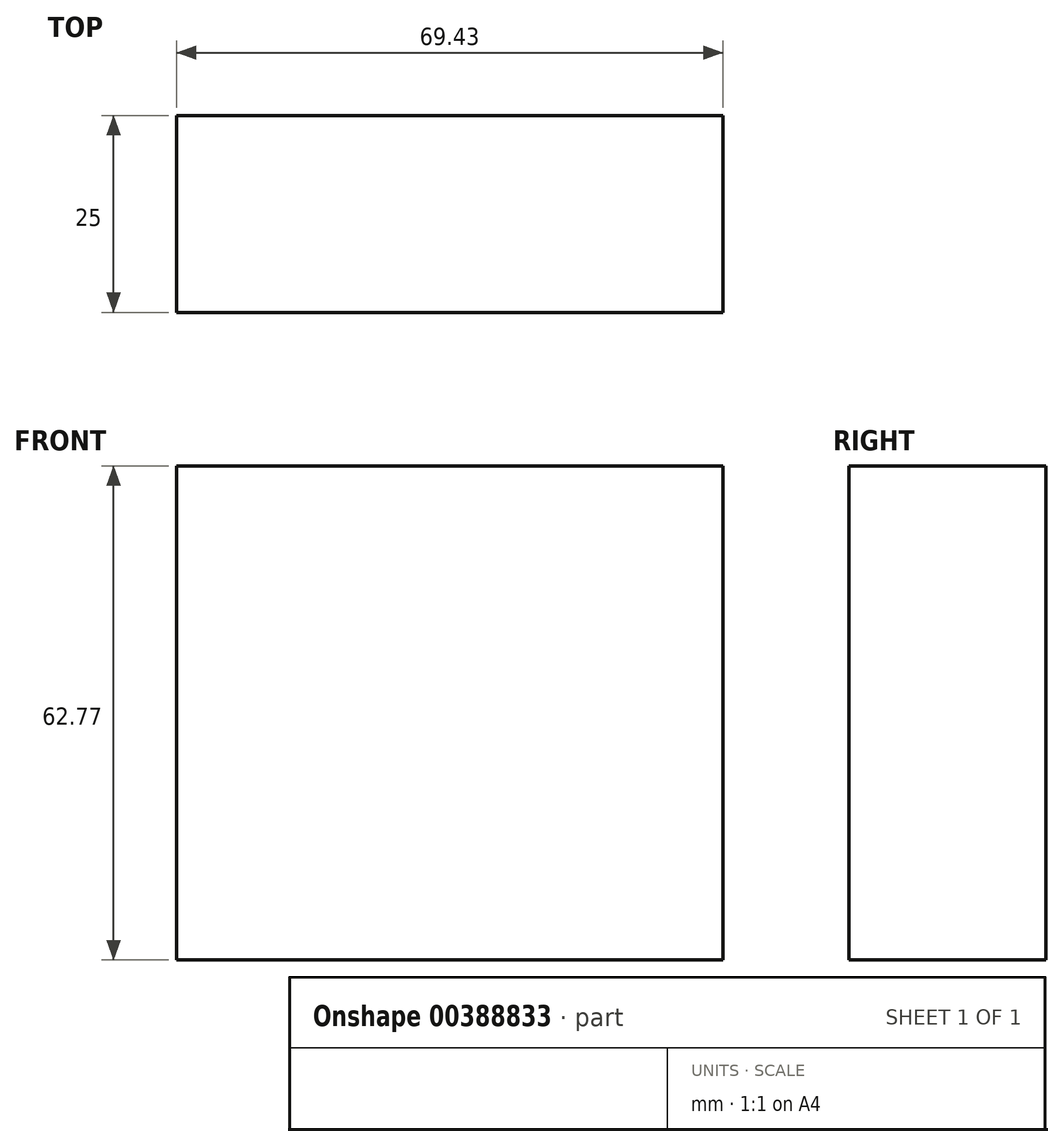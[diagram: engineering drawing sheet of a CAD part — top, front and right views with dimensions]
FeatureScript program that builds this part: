
annotation { "Feature Type Name" : "Feature", "Feature Type Description" : "" }
export const myFeature = defineFeature(function(context is Context, id is Id, definition is map)
    precondition{}
    {
        {
            var Q0;
            Q0=qCreatedBy(makeId("Front.planeOp"),FACE);
            var sketch = newSketch(context, id + "F0", { "sketchPlane" : qUnion([Q0])});
            skLineSegment(sketch, "E0.bottom", {"start": v(-106.48, 10.32) * mm, "end": v(-37.05, 10.32) * mm});
            skLineSegment(sketch, "E0.top", {"start": v(-106.48, 73.09) * mm, "end": v(-37.05, 73.09) * mm});
            skLineSegment(sketch, "E0.left", {"start": v(-106.48, 10.32) * mm, "end": v(-106.48, 73.09) * mm});
            skLineSegment(sketch, "E0.right", {"start": v(-37.05, 10.32) * mm, "end": v(-37.05, 73.09) * mm});
            skPoint(sketch, "E0.middle", {"position": v(-71.76, 41.7) * mm});
            skSolve(sketch);
        }
        {
            var Q0;
            Q0=makeQuery(id+"F0.imprint","IMPRINT",FACE,{"disambiguationData":[TD([[makeQuery(id+"F0.imprint","IMPRINT",EDGE,{"derivedFrom":sQuery(id+"F0.wireOp",EDGE,"E0.bottom")}),1.0]])]});
            extrude(context, id + "F1", {"entities" : qUnion([Q0]), "depth" : 25 * mm});
        }
    });
